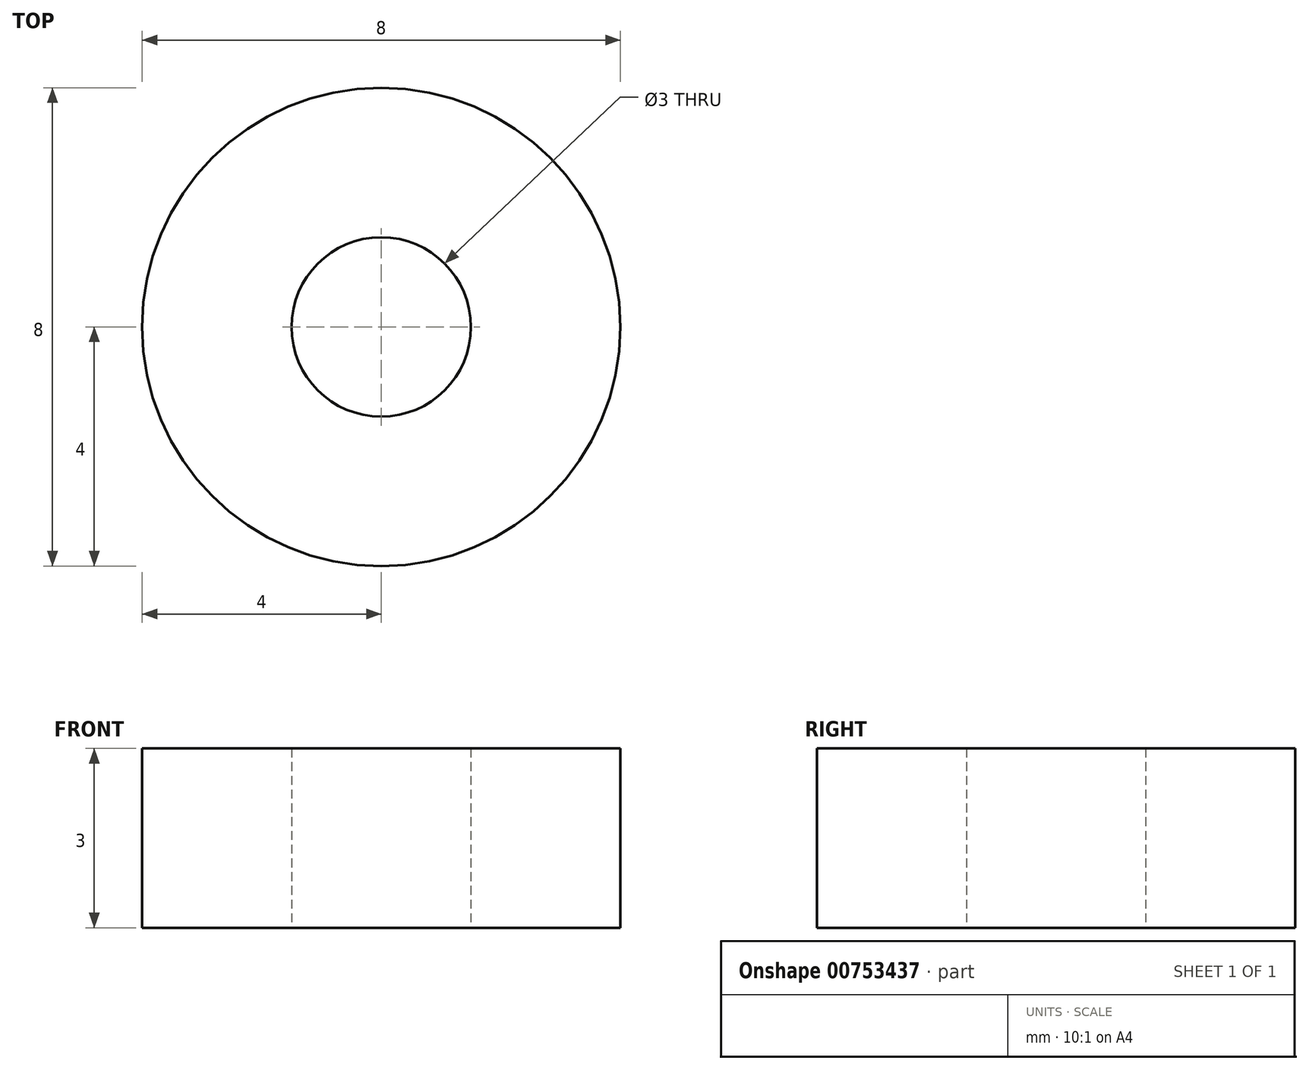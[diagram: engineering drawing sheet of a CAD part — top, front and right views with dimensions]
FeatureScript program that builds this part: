
annotation { "Feature Type Name" : "Feature", "Feature Type Description" : "" }
export const myFeature = defineFeature(function(context is Context, id is Id, definition is map)
    precondition{}
    {
        {
            var Q0;
            Q0=qCreatedBy(makeId("Top.planeOp"),FACE);
            var sketch = newSketch(context, id + "F0", { "sketchPlane" : qUnion([Q0])});
            skCircle(sketch, "E0", {"center": v(0, 0) * mm, "radius": 4 * mm});
            skCircle(sketch, "E1", {"center": v(0, 0) * mm, "radius": 1.5 * mm});
            skSolve(sketch);
        }
        {
            var Q0;
            Q0=makeQuery(id+"F0.imprint","IMPRINT",FACE,{"disambiguationData":[TD([[makeQuery(id+"F0.imprint","IMPRINT",EDGE,{"derivedFrom":sQuery(id+"F0.wireOp",EDGE,"E0")}),1.0]])]});
            extrude(context, id + "F1", {"entities" : qUnion([Q0]), "depth" : 3 * mm, "offsetDistance" : 25 * mm});
        }
    });
